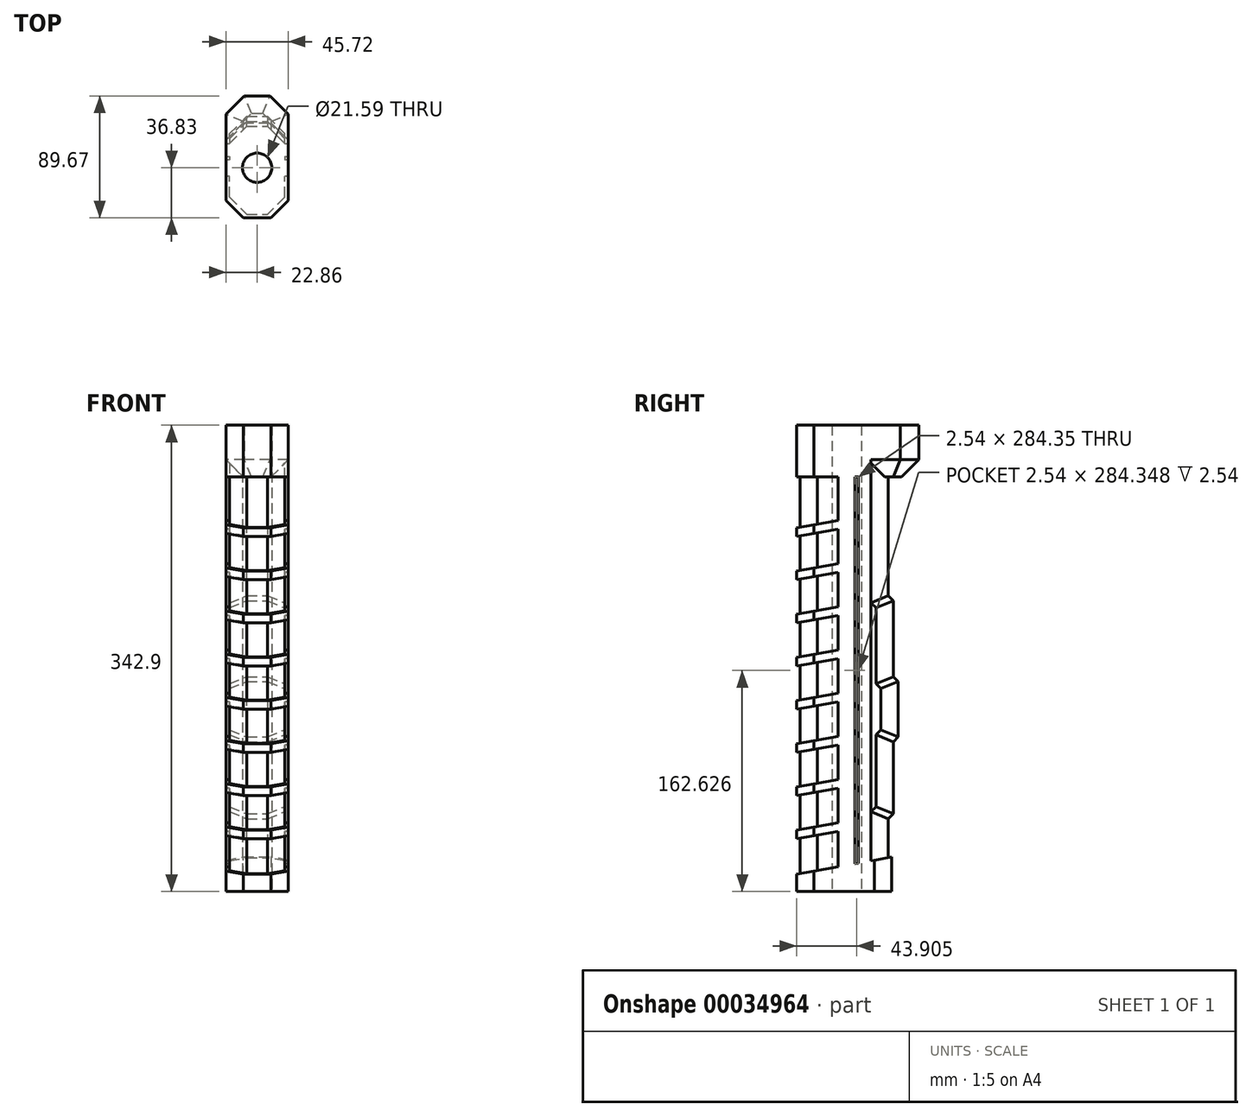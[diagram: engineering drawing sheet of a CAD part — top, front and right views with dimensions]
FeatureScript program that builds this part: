
annotation { "Feature Type Name" : "Feature", "Feature Type Description" : "" }
export const myFeature = defineFeature(function(context is Context, id is Id, definition is map)
    precondition{}
    {
        {
            var Q0;
            Q0=qCreatedBy(makeId("Top.planeOp"),FACE);
            var sketch = newSketch(context, id + "F0", { "sketchPlane" : qUnion([Q0])});
            skCircle(sketch, "E0", {"center": v(0, 0) * mm, "radius": 9.53 * mm});
            skSolve(sketch);
        }
        {
            var Q0;
            Q0=qSketchRegion(id+"F0",true);
            extrude(context, id + "F1", {"entities" : qUnion([Q0]), "depth" : 38.1 * mm});
        }
        {
            var Q0;
            Q0=makeQuery(id+"F1.opExtrude","CAP_FACE",FACE,{"disambiguationData":[OSD([sQuery(id+"F0.wireOp",EDGE,"E0")])],"isStart":false});
            var sketch = newSketch(context, id + "F2", { "sketchPlane" : qUnion([Q0])});
            skLineSegment(sketch, "E1.bottom", {"start": v(-22.86, -17.78) * mm, "end": v(22.86, -17.78) * mm});
            skLineSegment(sketch, "E1.top", {"start": v(-22.86, 52.07) * mm, "end": v(22.86, 52.07) * mm});
            skLineSegment(sketch, "E1.left", {"start": v(-22.86, -17.78) * mm, "end": v(-22.86, 52.07) * mm});
            skLineSegment(sketch, "E1.right", {"start": v(22.86, -17.78) * mm, "end": v(22.86, 52.07) * mm});
            skSolve(sketch);
        }
        {
            var Q0;
            Q0=makeQuery(id+"F2.imprint","IMPRINT",FACE,{"disambiguationData":[TD([[makeQuery(id+"F2.imprint","IMPRINT",EDGE,{"derivedFrom":sQuery(id+"F2.wireOp",EDGE,"7003b8e0-f063-402b-a916-a828eb53b423.0")}),-1.0]])]});
            var Q1;
            {var subQ0=makeQuery(id+"F1.opExtrude","CAP_EDGE",EDGE,{"disambiguationData":[OSD([sQuery(id+"F0.wireOp",EDGE,"E0")])],"isStart":false});var subQ1=sQuery(id+"F2.wireOp",EDGE,"b5096f53-b7b5-46b7-9458-e08269a2e02d");var subQ3=makeQuery(id+"F2.imprint","INTERSECT",VERTEX,{"disambiguationData":[OD(0.0)],"derivedFrom":[subQ0,subQ1]});Q1=makeQuery(id+"F2.imprint","IMPRINT",FACE,{"disambiguationData":[TD([[makeQuery(id+"F2.imprint","IMPRINT",EDGE,{"disambiguationData":[TD([[subQ3,-1.0]])],"derivedFrom":subQ1}),-1.0]])]});}
            var Q2;
            {var subQ4=sQuery(id+"F2.wireOp",EDGE,"7003b8e0-f063-402b-a916-a828eb53b423.2");Q2=makeQuery(id+"F2.imprint","IMPRINT",FACE,{"disambiguationData":[TD([[makeQuery(id+"F2.imprint","IMPRINT",EDGE,{"derivedFrom":subQ4}),-1.0]])]});}
            var Q3;
            {var subQ0=makeQuery(id+"F1.opExtrude","CAP_EDGE",EDGE,{"disambiguationData":[OSD([sQuery(id+"F0.wireOp",EDGE,"E0")])],"isStart":false});var subQ1=sQuery(id+"F2.wireOp",EDGE,"b5096f53-b7b5-46b7-9458-e08269a2e02d");var subQ3=makeQuery(id+"F2.imprint","INTERSECT",VERTEX,{"disambiguationData":[OD(0.0)],"derivedFrom":[subQ0,subQ1]});Q3=makeQuery(id+"F2.imprint","IMPRINT",FACE,{"disambiguationData":[TD([[makeQuery(id+"F2.imprint","IMPRINT",EDGE,{"disambiguationData":[TD([[subQ3,-1.0]])],"derivedFrom":subQ1}),1.0]])]});}
            var Q4;
            Q4=makeQuery(id+"F2.imprint","IMPRINT",FACE,{"disambiguationData":[TD([[makeQuery(id+"F2.imprint","IMPRINT",EDGE,{"derivedFrom":makeQuery(id+"F1.opExtrude","CAP_EDGE",EDGE,{"disambiguationData":[OSD([sQuery(id+"F0.wireOp",EDGE,"E0")])],"isStart":false})}),1.0]])]});
            var Q5;
            Q5=makeQuery(id+"F2.imprint","IMPRINT",FACE,{"disambiguationData":[TD([[makeQuery(id+"F2.imprint","IMPRINT",EDGE,{"derivedFrom":sQuery(id+"F2.wireOp",EDGE,"E1.bottom")}),1.0]])]});
            extrude(context, id + "F3", {"entities" : qUnion([Q0, Q1, Q2, Q3, Q4, Q5]), "operationType" : NewBodyOperationType.ADD, "depth" : 25.4 * mm});
        }
        {
            var Q0;
            Q0=makeQuery(id+"F3.opExtrude","SWEPT_EDGE",EDGE,{"disambiguationData":[OSD([sQuery(id+"F2.wireOp",EDGE,"E1.bottom"),sQuery(id+"F2.wireOp",EDGE,"E1.left")])]});
            var Q1;
            Q1=makeQuery(id+"F3.opExtrude","SWEPT_EDGE",EDGE,{"disambiguationData":[OSD([sQuery(id+"F2.wireOp",EDGE,"E1.top"),sQuery(id+"F2.wireOp",EDGE,"E1.left")])]});
            var Q2;
            Q2=makeQuery(id+"F3.opExtrude","SWEPT_EDGE",EDGE,{"disambiguationData":[OSD([sQuery(id+"F2.wireOp",EDGE,"E1.bottom"),sQuery(id+"F2.wireOp",EDGE,"E1.right")])]});
            var Q3;
            Q3=makeQuery(id+"F3.opExtrude","SWEPT_EDGE",EDGE,{"disambiguationData":[OSD([sQuery(id+"F2.wireOp",EDGE,"E1.top"),sQuery(id+"F2.wireOp",EDGE,"E1.right")])]});
            chamfer(context, id + "F4", {"entities" : qUnion([Q0, Q1, Q2, Q3]), "width" : 12.7 * mm, "tangentPropagation" : true});
        }
        {
            var Q0;
            Q0=qCreatedBy(makeId("Right.planeOp"),FACE);
            var sketch = newSketch(context, id + "F5", { "sketchPlane" : qUnion([Q0])});
            skLineSegment(sketch, "E2.0", {"start": v(-5.08, 63.5) * mm, "end": v(39.37, 63.5) * mm});
            skLineSegment(sketch, "E3.0", {"start": v(-5.08, 63.5) * mm, "end": v(-17.78, 63.5) * mm});
            skLineSegment(sketch, "E3.1", {"start": v(-17.78, 63.5) * mm, "end": v(-17.78, 38.1) * mm});
            skLineSegment(sketch, "E4.0", {"start": v(52.07, 63.5) * mm, "end": v(39.37, 63.5) * mm});
            skLineSegment(sketch, "E5", {"start": v(-17.78, 50.8) * mm, "end": v(52.07, 63.5) * mm});
            skSolve(sketch);
        }
        {
            var Q0;
            Q0=qSketchRegion(id+"F5",true);
            extrude(context, id + "F6", {"entities" : qUnion([Q0]), "operationType" : NewBodyOperationType.REMOVE, "endBound" : BoundingType.SYMMETRIC, "oppositeDirection" : true, "depth" : 50.8 * mm});
        }
        {
            var Q0;
            Q0=qCreatedBy(makeId("Right.planeOp"),FACE);
            var sketch = newSketch(context, id + "F7", { "sketchPlane" : qUnion([Q0])});
            skLineSegment(sketch, "E6.0", {"start": v(52.07, 38.1) * mm, "end": v(52.07, 63.5) * mm});
            skLineSegment(sketch, "E6.1", {"start": v(-17.78, 50.8) * mm, "end": v(-17.78, 38.1) * mm});
            skLineSegment(sketch, "E6.2", {"start": v(-5.08, 38.1) * mm, "end": v(39.37, 38.1) * mm});
            skLineSegment(sketch, "E6.3", {"start": v(-17.78, 38.1) * mm, "end": v(-5.08, 38.1) * mm});
            skLineSegment(sketch, "E6.4", {"start": v(39.37, 38.1) * mm, "end": v(52.07, 38.1) * mm});
            skLineSegment(sketch, "E7", {"start": v(-15.24, 38.1) * mm, "end": v(-15.24, 342.9) * mm});
            skLineSegment(sketch, "E8", {"start": v(49.53, 38.1) * mm, "end": v(49.53, 91.66) * mm});
            skPoint(sketch, "E9.orphan", {"position": v(49.53, 0) * mm});
            skLineSegment(sketch, "E10", {"start": v(-15.24, 342.9) * mm, "end": v(49.53, 342.9) * mm});
            skLineSegment(sketch, "E11", {"start": v(49.53, 91.66) * mm, "end": v(53.12, 95.25) * mm});
            skLineSegment(sketch, "E12", {"start": v(53.12, 95.25) * mm, "end": v(53.12, 148.19) * mm});
            skLineSegment(sketch, "E13", {"start": v(53.12, 148.19) * mm, "end": v(56.71, 151.78) * mm});
            skLineSegment(sketch, "E14", {"start": v(56.71, 151.78) * mm, "end": v(56.71, 192.57) * mm});
            skLineSegment(sketch, "E15", {"start": v(56.71, 192.57) * mm, "end": v(53.12, 196.16) * mm});
            skLineSegment(sketch, "E16", {"start": v(53.12, 196.16) * mm, "end": v(53.12, 252) * mm});
            skLineSegment(sketch, "E17", {"start": v(53.12, 252) * mm, "end": v(49.53, 255.6) * mm});
            skLineSegment(sketch, "E18.trimOffspring", {"start": v(49.53, 255.6) * mm, "end": v(49.53, 342.9) * mm});
            skSolve(sketch);
        }
        {
            var Q0;
            {var subQ3=sQuery(id+"F7.wireOp",EDGE,"E6.2");Q0=makeQuery(id+"F7.imprint","IMPRINT",FACE,{"disambiguationData":[TD([[makeQuery(id+"F7.imprint","IMPRINT",EDGE,{"derivedFrom":subQ3}),1.0]])]});}
            extrude(context, id + "F8", {"entities" : qUnion([Q0]), "operationType" : NewBodyOperationType.ADD, "endBound" : BoundingType.SYMMETRIC, "oppositeDirection" : true, "depth" : 40.64 * mm});
        }
        {
            var Q0;
            Q0=makeQuery(id+"F8.opExtrude","CAP_EDGE",EDGE,{"disambiguationData":[OSD([sQuery(id+"F7.wireOp",EDGE,"E8")])],"isStart":false});
            var Q1;
            Q1=makeQuery(id+"F8.opExtrude","CAP_EDGE",EDGE,{"disambiguationData":[OSD([sQuery(id+"F7.wireOp",EDGE,"E8")])],"isStart":true});
            var Q2;
            Q2=makeQuery(id+"F8.opExtrude","CAP_EDGE",EDGE,{"disambiguationData":[OSD([sQuery(id+"F7.wireOp",EDGE,"E7")])],"isStart":false});
            var Q3;
            Q3=makeQuery(id+"F8.opExtrude","CAP_EDGE",EDGE,{"disambiguationData":[OSD([sQuery(id+"F7.wireOp",EDGE,"E7")])],"isStart":true});
            var Q4;
            Q4=makeQuery(id+"F8.opExtrude","CAP_EDGE",EDGE,{"disambiguationData":[OSD([sQuery(id+"F7.wireOp",EDGE,"E18.trimOffspring")])],"isStart":false});
            var Q5;
            Q5=makeQuery(id+"F8.opExtrude","CAP_EDGE",EDGE,{"disambiguationData":[OSD([sQuery(id+"F7.wireOp",EDGE,"E18.trimOffspring")])],"isStart":true});
            var Q6;
            Q6=makeQuery(id+"F8.opExtrude","CAP_EDGE",EDGE,{"disambiguationData":[OSD([sQuery(id+"F7.wireOp",EDGE,"E12")])],"isStart":false});
            var Q7;
            Q7=makeQuery(id+"F8.opExtrude","CAP_EDGE",EDGE,{"disambiguationData":[OSD([sQuery(id+"F7.wireOp",EDGE,"E11")])],"isStart":false});
            var Q8;
            Q8=makeQuery(id+"F8.opExtrude","CAP_EDGE",EDGE,{"disambiguationData":[OSD([sQuery(id+"F7.wireOp",EDGE,"E14")])],"isStart":false});
            var Q9;
            Q9=makeQuery(id+"F8.opExtrude","CAP_EDGE",EDGE,{"disambiguationData":[OSD([sQuery(id+"F7.wireOp",EDGE,"E13")])],"isStart":false});
            var Q10;
            Q10=makeQuery(id+"F8.opExtrude","CAP_EDGE",EDGE,{"disambiguationData":[OSD([sQuery(id+"F7.wireOp",EDGE,"E15")])],"isStart":false});
            var Q11;
            Q11=makeQuery(id+"F8.opExtrude","CAP_EDGE",EDGE,{"disambiguationData":[OSD([sQuery(id+"F7.wireOp",EDGE,"E16")])],"isStart":false});
            var Q12;
            Q12=makeQuery(id+"F8.opExtrude","CAP_EDGE",EDGE,{"disambiguationData":[OSD([sQuery(id+"F7.wireOp",EDGE,"E17")])],"isStart":false});
            var Q13;
            Q13=makeQuery(id+"F8.opExtrude","CAP_EDGE",EDGE,{"disambiguationData":[OSD([sQuery(id+"F7.wireOp",EDGE,"E11")])],"isStart":true});
            var Q14;
            Q14=makeQuery(id+"F8.opExtrude","CAP_EDGE",EDGE,{"disambiguationData":[OSD([sQuery(id+"F7.wireOp",EDGE,"E12")])],"isStart":true});
            var Q15;
            Q15=makeQuery(id+"F8.opExtrude","CAP_EDGE",EDGE,{"disambiguationData":[OSD([sQuery(id+"F7.wireOp",EDGE,"E13")])],"isStart":true});
            var Q16;
            Q16=makeQuery(id+"F8.opExtrude","CAP_EDGE",EDGE,{"disambiguationData":[OSD([sQuery(id+"F7.wireOp",EDGE,"E14")])],"isStart":true});
            var Q17;
            Q17=makeQuery(id+"F8.opExtrude","CAP_EDGE",EDGE,{"disambiguationData":[OSD([sQuery(id+"F7.wireOp",EDGE,"E15")])],"isStart":true});
            var Q18;
            Q18=makeQuery(id+"F8.opExtrude","CAP_EDGE",EDGE,{"disambiguationData":[OSD([sQuery(id+"F7.wireOp",EDGE,"E16")])],"isStart":true});
            var Q19;
            Q19=makeQuery(id+"F8.opExtrude","CAP_EDGE",EDGE,{"disambiguationData":[OSD([sQuery(id+"F7.wireOp",EDGE,"E17")])],"isStart":true});
            chamfer(context, id + "F9", {"entities" : qUnion([Q0, Q1, Q2, Q3, Q4, Q5, Q6, Q7, Q8, Q9, Q10, Q11, Q12, Q13, Q14, Q15, Q16, Q17, Q18, Q19]), "width" : 12.7 * mm, "tangentPropagation" : true});
        }
        {
            var Q0;
            Q0=qCreatedBy(makeId("Right.planeOp"),FACE);
            var sketch = newSketch(context, id + "F10", { "sketchPlane" : qUnion([Q0])});
            skLineSegment(sketch, "E19.0", {"start": v(-5.08, 38.1) * mm, "end": v(39.37, 38.1) * mm});
            skLineSegment(sketch, "E19.1", {"start": v(-15.24, 38.1) * mm, "end": v(-5.08, 38.1) * mm});
            skLineSegment(sketch, "E19.2", {"start": v(41.91, 38.1) * mm, "end": v(52.07, 38.1) * mm});
            skLineSegment(sketch, "E19.3", {"start": v(-17.78, 50.8) * mm, "end": v(-17.78, 38.1) * mm});
            skLineSegment(sketch, "E20.0", {"start": v(36.83, 342.9) * mm, "end": v(36.83, 250.33) * mm});
            skLineSegment(sketch, "E21", {"start": v(12.7, 82.42) * mm, "end": v(-17.78, 76.87) * mm});
            skLineSegment(sketch, "E22", {"start": v(-17.78, 76.87) * mm, "end": v(-17.78, 83.21) * mm});
            skLineSegment(sketch, "E23", {"start": v(-17.78, 83.21) * mm, "end": v(12.7, 88.75) * mm});
            skLineSegment(sketch, "E24", {"start": v(12.7, 38.1) * mm, "end": v(12.7, 82.42) * mm});
            skLineSegment(sketch, "E25.trimOffspring", {"start": v(12.7, 88.75) * mm, "end": v(12.7, 114.17) * mm});
            skLineSegment(sketch, "E26.0.1.0", {"start": v(12.7, 114.17) * mm, "end": v(-17.78, 108.62) * mm});
            skLineSegment(sketch, "E26.0.1.1", {"start": v(-17.78, 114.96) * mm, "end": v(12.7, 120.5) * mm});
            skLineSegment(sketch, "E26.0.1.2", {"start": v(-17.78, 108.62) * mm, "end": v(-17.78, 114.96) * mm});
            skLineSegment(sketch, "E26.0.2.0", {"start": v(12.7, 145.92) * mm, "end": v(-17.78, 140.37) * mm});
            skLineSegment(sketch, "E26.0.2.1", {"start": v(-17.78, 146.71) * mm, "end": v(12.7, 152.25) * mm});
            skLineSegment(sketch, "E26.0.2.2", {"start": v(-17.78, 140.37) * mm, "end": v(-17.78, 146.71) * mm});
            skLineSegment(sketch, "E26.0.3.0", {"start": v(12.7, 177.67) * mm, "end": v(-17.78, 172.12) * mm});
            skLineSegment(sketch, "E26.0.3.1", {"start": v(-17.78, 178.46) * mm, "end": v(12.7, 184) * mm});
            skLineSegment(sketch, "E26.0.3.2", {"start": v(-17.78, 172.12) * mm, "end": v(-17.78, 178.46) * mm});
            skLineSegment(sketch, "E26.0.4.0", {"start": v(12.7, 209.42) * mm, "end": v(-17.78, 203.87) * mm});
            skLineSegment(sketch, "E26.0.4.1", {"start": v(-17.78, 210.21) * mm, "end": v(12.7, 215.75) * mm});
            skLineSegment(sketch, "E26.0.4.2", {"start": v(-17.78, 203.87) * mm, "end": v(-17.78, 210.21) * mm});
            skLineSegment(sketch, "E26.0.5.0", {"start": v(12.7, 241.17) * mm, "end": v(-17.78, 235.62) * mm});
            skLineSegment(sketch, "E26.0.5.1", {"start": v(-17.78, 241.96) * mm, "end": v(12.7, 247.5) * mm});
            skLineSegment(sketch, "E26.0.5.2", {"start": v(-17.78, 235.62) * mm, "end": v(-17.78, 241.96) * mm});
            skLineSegment(sketch, "E26.0.6.0", {"start": v(12.7, 272.92) * mm, "end": v(-17.78, 267.37) * mm});
            skLineSegment(sketch, "E26.0.6.1", {"start": v(-17.78, 273.71) * mm, "end": v(12.7, 279.25) * mm});
            skLineSegment(sketch, "E26.0.6.2", {"start": v(-17.78, 267.37) * mm, "end": v(-17.78, 273.71) * mm});
            skLineSegment(sketch, "E26.0.7.0", {"start": v(12.7, 304.67) * mm, "end": v(-17.78, 299.12) * mm});
            skLineSegment(sketch, "E26.0.7.1", {"start": v(-17.78, 305.46) * mm, "end": v(12.7, 311) * mm});
            skLineSegment(sketch, "E26.0.7.2", {"start": v(-17.78, 299.12) * mm, "end": v(-17.78, 305.46) * mm});
            skLineSegment(sketch, "E26.0.7.3", {"start": v(36.83, 260.35) * mm, "end": v(36.83, 342.9) * mm});
            skLineSegment(sketch, "E26.direction1", {"start": v(-17.78, 76.87) * mm, "end": v(7.62, 76.87) * mm, "construction": true});
            skLineSegment(sketch, "E26.direction2", {"start": v(-17.78, 76.87) * mm, "end": v(-17.78, 108.62) * mm, "construction": true});
            skLineSegment(sketch, "E27.trimOffspring", {"start": v(12.7, 120.5) * mm, "end": v(12.7, 145.92) * mm});
            skLineSegment(sketch, "E28.trimOffspring", {"start": v(12.7, 152.25) * mm, "end": v(12.7, 177.67) * mm});
            skLineSegment(sketch, "E29.trimOffspring", {"start": v(12.7, 184) * mm, "end": v(12.7, 209.42) * mm});
            skLineSegment(sketch, "E30.trimOffspring", {"start": v(12.7, 215.75) * mm, "end": v(12.7, 241.17) * mm});
            skLineSegment(sketch, "E31.trimOffspring", {"start": v(12.7, 247.5) * mm, "end": v(12.7, 272.92) * mm});
            skLineSegment(sketch, "E32.trimOffspring", {"start": v(12.7, 279.25) * mm, "end": v(12.7, 304.67) * mm});
            skLineSegment(sketch, "E33.trimOffspring", {"start": v(12.7, 311) * mm, "end": v(12.7, 342.9) * mm});
            skLineSegment(sketch, "E34", {"start": v(36.83, 342.9) * mm, "end": v(12.7, 342.9) * mm});
            skLineSegment(sketch, "E35", {"start": v(36.83, 342.9) * mm, "end": v(36.83, 38.1) * mm});
            skLineSegment(sketch, "E36", {"start": v(24.85, 38.1) * mm, "end": v(24.85, 350.34) * mm});
            skLineSegment(sketch, "E37", {"start": v(24.85, 350.34) * mm, "end": v(27.4, 350.34) * mm});
            skLineSegment(sketch, "E38", {"start": v(27.4, 350.34) * mm, "end": v(27.4, 38.1) * mm});
            skSolve(sketch);
        }
        {
            var Q0;
            Q0=makeQuery(id+"F10.imprint","IMPRINT",FACE,{"disambiguationData":[TD([[makeQuery(id+"F10.imprint","IMPRINT",EDGE,{"derivedFrom":sQuery(id+"F10.wireOp",EDGE,"E21")}),-1.0]])]});
            var Q1;
            {var subQ3=sQuery(id+"F10.wireOp",EDGE,"E19.0");var subQ5=sQuery(id+"F10.wireOp",EDGE,"E35");var subQ6=makeQuery(id+"F10.imprint","INTERSECT",VERTEX,{"derivedFrom":[subQ3,subQ5]});Q1=makeQuery(id+"F10.imprint","IMPRINT",FACE,{"disambiguationData":[TD([[makeQuery(id+"F10.imprint","IMPRINT",EDGE,{"disambiguationData":[TD([[subQ6,1.0]])],"derivedFrom":subQ3}),1.0]])]});}
            extrude(context, id + "F11", {"entities" : qUnion([Q0, Q1]), "operationType" : NewBodyOperationType.ADD, "endBound" : BoundingType.SYMMETRIC, "depth" : 45.72 * mm});
        }
        {
            var Q0;
            Q0=makeQuery(id+"F11.opExtrude","CAP_EDGE",EDGE,{"disambiguationData":[OSD([sQuery(id+"F10.wireOp",EDGE,"E26.0.7.2")])],"isStart":true});
            var Q1;
            Q1=makeQuery(id+"F11.opExtrude","CAP_EDGE",EDGE,{"disambiguationData":[OSD([sQuery(id+"F10.wireOp",EDGE,"E26.0.6.2")])],"isStart":true});
            var Q2;
            Q2=makeQuery(id+"F11.opExtrude","CAP_EDGE",EDGE,{"disambiguationData":[OSD([sQuery(id+"F10.wireOp",EDGE,"E26.0.5.2")])],"isStart":true});
            var Q3;
            Q3=makeQuery(id+"F11.opExtrude","CAP_EDGE",EDGE,{"disambiguationData":[OSD([sQuery(id+"F10.wireOp",EDGE,"E26.0.4.2")])],"isStart":true});
            var Q4;
            Q4=makeQuery(id+"F11.opExtrude","CAP_EDGE",EDGE,{"disambiguationData":[OSD([sQuery(id+"F10.wireOp",EDGE,"E26.0.3.2")])],"isStart":true});
            var Q5;
            Q5=makeQuery(id+"F11.opExtrude","CAP_EDGE",EDGE,{"disambiguationData":[OSD([sQuery(id+"F10.wireOp",EDGE,"E26.0.2.2")])],"isStart":true});
            var Q6;
            Q6=makeQuery(id+"F11.opExtrude","CAP_EDGE",EDGE,{"disambiguationData":[OSD([sQuery(id+"F10.wireOp",EDGE,"E26.0.1.2")])],"isStart":true});
            var Q7;
            Q7=makeQuery(id+"F11.opExtrude","CAP_EDGE",EDGE,{"disambiguationData":[OSD([sQuery(id+"F10.wireOp",EDGE,"E22")])],"isStart":true});
            var Q8;
            Q8=makeQuery(id+"F11.opExtrude","CAP_EDGE",EDGE,{"disambiguationData":[OSD([sQuery(id+"F10.wireOp",EDGE,"E22")])],"isStart":false});
            var Q9;
            Q9=makeQuery(id+"F11.opExtrude","CAP_EDGE",EDGE,{"disambiguationData":[OSD([sQuery(id+"F10.wireOp",EDGE,"E26.0.1.2")])],"isStart":false});
            var Q10;
            Q10=makeQuery(id+"F11.opExtrude","CAP_EDGE",EDGE,{"disambiguationData":[OSD([sQuery(id+"F10.wireOp",EDGE,"E26.0.2.2")])],"isStart":false});
            var Q11;
            Q11=makeQuery(id+"F11.opExtrude","CAP_EDGE",EDGE,{"disambiguationData":[OSD([sQuery(id+"F10.wireOp",EDGE,"E26.0.3.2")])],"isStart":false});
            var Q12;
            Q12=makeQuery(id+"F11.opExtrude","CAP_EDGE",EDGE,{"disambiguationData":[OSD([sQuery(id+"F10.wireOp",EDGE,"E26.0.4.2")])],"isStart":false});
            var Q13;
            Q13=makeQuery(id+"F11.opExtrude","CAP_EDGE",EDGE,{"disambiguationData":[OSD([sQuery(id+"F10.wireOp",EDGE,"E26.0.5.2")])],"isStart":false});
            var Q14;
            Q14=makeQuery(id+"F11.opExtrude","CAP_EDGE",EDGE,{"disambiguationData":[OSD([sQuery(id+"F10.wireOp",EDGE,"E26.0.6.2")])],"isStart":false});
            var Q15;
            Q15=makeQuery(id+"F11.opExtrude","CAP_EDGE",EDGE,{"disambiguationData":[OSD([sQuery(id+"F10.wireOp",EDGE,"E26.0.7.2")])],"isStart":false});
            chamfer(context, id + "F12", {"entities" : qUnion([Q0, Q1, Q2, Q3, Q4, Q5, Q6, Q7, Q8, Q9, Q10, Q11, Q12, Q13, Q14, Q15]), "width" : 12.7 * mm, "tangentPropagation" : true});
        }
        {
            var Q0;
            {var subQ0=sQuery(id+"F10.wireOp",EDGE,"E34");Q0=makeQuery(id+"F11.boolean.opBoolean","MERGE",FACE,{"derivedFrom":[makeQuery(id+"F8.opExtrude","SWEPT_FACE",FACE,{"disambiguationData":[OSD([sQuery(id+"F7.wireOp",EDGE,"E10")])]}),makeQuery(id+"F11.opExtrude","SWEPT_FACE",FACE,{"disambiguationData":[OSD([subQ0]),TDD([makeQuery(id+"F10.imprint","IMPRINT",EDGE,{"disambiguationData":[TD([[makeQuery(id+"F10.imprint","INTERSECT",VERTEX,{"derivedFrom":[subQ0,sQuery(id+"F10.wireOp",EDGE,"E35")]}),-1.0]])],"derivedFrom":subQ0})])]}),makeQuery(id+"F11.opExtrude","SWEPT_FACE",FACE,{"disambiguationData":[OSD([subQ0]),TDD([makeQuery(id+"F10.imprint","IMPRINT",EDGE,{"disambiguationData":[TD([[makeQuery(id+"F10.imprint","INTERSECT",VERTEX,{"derivedFrom":[sQuery(id+"F10.wireOp",EDGE,"E33.trimOffspring"),subQ0]}),1.0]])],"derivedFrom":subQ0})])]})]});}
            var sketch = newSketch(context, id + "F13", { "sketchPlane" : qUnion([Q0])});
            skLineSegment(sketch, "E39.0", {"start": v(-22.86, -5.08) * mm, "end": v(-22.86, 39.37) * mm});
            skLineSegment(sketch, "E39.1", {"start": v(-20.32, 41.91) * mm, "end": v(-10.16, 52.07) * mm});
            skLineSegment(sketch, "E40.0", {"start": v(-12.7, -15.24) * mm, "end": v(-22.86, -5.08) * mm});
            skLineSegment(sketch, "E40.1", {"start": v(-10.16, -17.78) * mm, "end": v(10.16, -17.78) * mm});
            skLineSegment(sketch, "E40.2", {"start": v(20.32, -7.62) * mm, "end": v(10.16, -17.78) * mm});
            skLineSegment(sketch, "E41.0", {"start": v(22.86, -5.08) * mm, "end": v(22.86, 39.37) * mm});
            skLineSegment(sketch, "E41.1", {"start": v(12.7, 49.53) * mm, "end": v(22.86, 39.37) * mm});
            skLineSegment(sketch, "E42", {"start": v(-22.86, -5.08) * mm, "end": v(-22.86, 58.42) * mm});
            skLineSegment(sketch, "E43", {"start": v(-22.86, 58.42) * mm, "end": v(-9.39, 71.9) * mm});
            skLineSegment(sketch, "E44", {"start": v(-9.39, 71.9) * mm, "end": v(9.39, 71.9) * mm});
            skLineSegment(sketch, "E45", {"start": v(9.39, 71.9) * mm, "end": v(22.86, 58.42) * mm});
            skLineSegment(sketch, "E46", {"start": v(22.86, -5.08) * mm, "end": v(22.86, 58.42) * mm});
            skLineSegment(sketch, "E47", {"start": v(-22.86, -5.08) * mm, "end": v(-10.16, -17.78) * mm});
            skLineSegment(sketch, "E48", {"start": v(10.16, -17.78) * mm, "end": v(22.86, -5.08) * mm});
            skPoint(sketch, "E39.2.end.orphan", {"position": v(10.16, 52.07) * mm});
            skSolve(sketch);
        }
        {
            var Q0;
            {var subQ52=sQuery(id+"F13.wireOp",EDGE,"E43");Q0=makeQuery(id+"F13.imprint","IMPRINT",FACE,{"disambiguationData":[TD([[makeQuery(id+"F13.imprint","IMPRINT",EDGE,{"derivedFrom":subQ52}),-1.0]])]});}
            var Q1;
            {var subQ46=sQuery(id+"F7.wireOp",EDGE,"E10");var subQ55=sQuery(id+"F7.wireOp",EDGE,"E7");Q1=makeQuery(id+"F13.imprint","IMPRINT",FACE,{"disambiguationData":[TD([[makeQuery(id+"F13.imprint","IMPRINT",EDGE,{"derivedFrom":makeQuery(id+"F8.opExtrude","SWEPT_EDGE",EDGE,{"disambiguationData":[OSD([subQ55,subQ46])]})}),1.0]])]});}
            var Q2;
            {var subQ63=sQuery(id+"F13.wireOp",EDGE,"E40.1");Q2=makeQuery(id+"F13.imprint","IMPRINT",FACE,{"disambiguationData":[TD([[makeQuery(id+"F13.imprint","IMPRINT",EDGE,{"derivedFrom":subQ63}),1.0]])]});}
            var Q3;
            {var subQ1=sQuery(id+"F10.wireOp",EDGE,"E36");var subQ2=makeQuery(id+"F11.opExtrude","SWEPT_FACE",FACE,{"disambiguationData":[OSD([subQ1])]});var subQ11=sQuery(id+"F7.wireOp",EDGE,"E10");Q3=makeQuery(id+"F13.imprint","IMPRINT",FACE,{"disambiguationData":[TD([[makeQuery(id+"F13.imprint","IMPRINT",EDGE,{"derivedFrom":makeQuery(id+"F11.boolean.opBoolean","SPLIT",EDGE,{"disambiguationData":[TD([subQ2])],"derivedFrom":makeQuery(id+"F8.opExtrude","CAP_EDGE",EDGE,{"disambiguationData":[OSD([subQ11])],"isStart":false})})}),1.0]])]});}
            var Q4;
            {var subQ1=sQuery(id+"F10.wireOp",EDGE,"E36");var subQ2=makeQuery(id+"F11.opExtrude","SWEPT_FACE",FACE,{"disambiguationData":[OSD([subQ1])]});var subQ11=sQuery(id+"F7.wireOp",EDGE,"E10");Q4=makeQuery(id+"F13.imprint","IMPRINT",FACE,{"disambiguationData":[TD([[makeQuery(id+"F13.imprint","IMPRINT",EDGE,{"derivedFrom":makeQuery(id+"F11.boolean.opBoolean","SPLIT",EDGE,{"disambiguationData":[TD([subQ2])],"derivedFrom":makeQuery(id+"F8.opExtrude","CAP_EDGE",EDGE,{"disambiguationData":[OSD([subQ11])],"isStart":true})})}),-1.0]])]});}
            extrude(context, id + "F14", {"entities" : qUnion([Q0, Q1, Q2, Q3, Q4]), "operationType" : NewBodyOperationType.ADD, "depth" : 38.1 * mm});
        }
        {
            var Q0;
            Q0=makeQuery(id+"F14.opExtrude","CAP_EDGE",EDGE,{"disambiguationData":[OSD([sQuery(id+"F13.wireOp",EDGE,"E44")])],"isStart":true});
            var Q1;
            {var subQ0=sQuery(id+"F13.wireOp",EDGE,"E46");var subQ2=sQuery(id+"F10.wireOp",EDGE,"E35");Q1=makeQuery(id+"F14.boolean.opBoolean","SPLIT",EDGE,{"disambiguationData":[TD([makeQuery(id+"F11.opExtrude","SWEPT_FACE",FACE,{"disambiguationData":[OSD([subQ2])]})])],"derivedFrom":makeQuery(id+"F14.opExtrude","CAP_EDGE",EDGE,{"disambiguationData":[OSD([subQ0])],"isStart":true})});}
            var Q2;
            {var subQ0=sQuery(id+"F13.wireOp",EDGE,"E42");var subQ2=sQuery(id+"F10.wireOp",EDGE,"E35");Q2=makeQuery(id+"F14.boolean.opBoolean","SPLIT",EDGE,{"disambiguationData":[TD([makeQuery(id+"F11.opExtrude","SWEPT_FACE",FACE,{"disambiguationData":[OSD([subQ2])]})])],"derivedFrom":makeQuery(id+"F14.opExtrude","CAP_EDGE",EDGE,{"disambiguationData":[OSD([subQ0])],"isStart":true})});}
            var Q3;
            Q3=makeQuery(id+"F14.opExtrude","CAP_EDGE",EDGE,{"disambiguationData":[OSD([sQuery(id+"F13.wireOp",EDGE,"E43")])],"isStart":true});
            var Q4;
            Q4=makeQuery(id+"F14.opExtrude","CAP_EDGE",EDGE,{"disambiguationData":[OSD([sQuery(id+"F13.wireOp",EDGE,"E45")])],"isStart":true});
            chamfer(context, id + "F15", {"entities" : qUnion([Q0, Q1, Q2, Q3, Q4]), "width" : 12.7 * mm, "tangentPropagation" : true});
        }
        {
            var Q0;
            Q0=makeQuery(id+"F14.opExtrude","CAP_FACE",FACE,{"disambiguationData":[OSD([sQuery(id+"F13.wireOp",EDGE,"E42"),sQuery(id+"F13.wireOp",EDGE,"E43"),sQuery(id+"F13.wireOp",EDGE,"E44"),sQuery(id+"F13.wireOp",EDGE,"E45"),sQuery(id+"F13.wireOp",EDGE,"E46"),sQuery(id+"F13.wireOp",EDGE,"E47"),sQuery(id+"F13.wireOp",EDGE,"E48"),sQuery(id+"F13.wireOp",EDGE,"E40.1")])],"isStart":false});
            var sketch = newSketch(context, id + "F16", { "sketchPlane" : qUnion([Q0])});
            skCircle(sketch, "E49", {"center": v(0, 31.75) * mm, "radius": 10.16 * mm});
            skSolve(sketch);
        }
        {
            var Q0;
            Q0=makeQuery(id+"F16.imprint","IMPRINT",FACE,{"disambiguationData":[TD([[makeQuery(id+"F16.imprint","IMPRINT",EDGE,{"derivedFrom":sQuery(id+"F16.wireOp",EDGE,"E49")}),1.0]])]});
            extrude(context, id + "F17", {"entities" : qUnion([Q0]), "operationType" : NewBodyOperationType.REMOVE, "oppositeDirection" : true, "depth" : 38.1 * mm});
        }
        {
            var Q0;
            Q0=makeQuery(id+"F1.opExtrude","CAP_FACE",FACE,{"disambiguationData":[OSD([sQuery(id+"F0.wireOp",EDGE,"E0")])],"isStart":true});
            extrude(context, id + "F18", {"entities" : qUnion([Q0]), "operationType" : NewBodyOperationType.REMOVE, "oppositeDirection" : true, "depth" : 38.1 * mm});
        }
        {
            var Q0;
            Q0=makeQuery(id+"F17.boolean.opBoolean","COPY",FACE,{"derivedFrom":makeQuery(id+"F17.opExtrude","CAP_FACE",FACE,{"disambiguationData":[OSD([sQuery(id+"F16.wireOp",EDGE,"E49")])],"isStart":false})});
            extrude(context, id + "F19", {"entities" : qUnion([Q0]), "operationType" : NewBodyOperationType.ADD, "depth" : 38.1 * mm});
        }
        {
            var Q0;
            Q0=makeQuery(id+"F18.boolean.opBoolean","MERGE",FACE,{"derivedFrom":[makeQuery(id+"F8.boolean.opBoolean","MERGE",FACE,{"derivedFrom":[makeQuery(id+"F3.opExtrude","CAP_FACE",FACE,{"disambiguationData":[OSD([sQuery(id+"F2.wireOp",EDGE,"E1.bottom"),sQuery(id+"F2.wireOp",EDGE,"E1.top"),sQuery(id+"F2.wireOp",EDGE,"E1.left"),sQuery(id+"F2.wireOp",EDGE,"E1.right")])],"isStart":true}),makeQuery(id+"F8.opExtrude","SWEPT_FACE",FACE,{"disambiguationData":[OSD([sQuery(id+"F7.wireOp",EDGE,"E6.2"),sQuery(id+"F7.wireOp",EDGE,"E6.3"),sQuery(id+"F7.wireOp",EDGE,"E6.4")])]})]}),makeQuery(id+"F18.opExtrude","CAP_FACE",FACE,{"disambiguationData":[OSD([sQuery(id+"F0.wireOp",EDGE,"E0")])],"isStart":false})]});
            var sketch = newSketch(context, id + "F20", { "sketchPlane" : qUnion([Q0])});
            skCircle(sketch, "E50", {"center": v(0, -19.05) * mm, "radius": 10.8 * mm});
            skSolve(sketch);
        }
        {
            var Q0;
            Q0=makeQuery(id+"F20.imprint","IMPRINT",FACE,{"disambiguationData":[TD([[makeQuery(id+"F20.imprint","IMPRINT",EDGE,{"derivedFrom":sQuery(id+"F20.wireOp",EDGE,"E50")}),1.0]])]});
            extrude(context, id + "F21", {"entities" : qUnion([Q0]), "operationType" : NewBodyOperationType.REMOVE, "oppositeDirection" : true, "depth" : 508 * mm});
        }
    });
